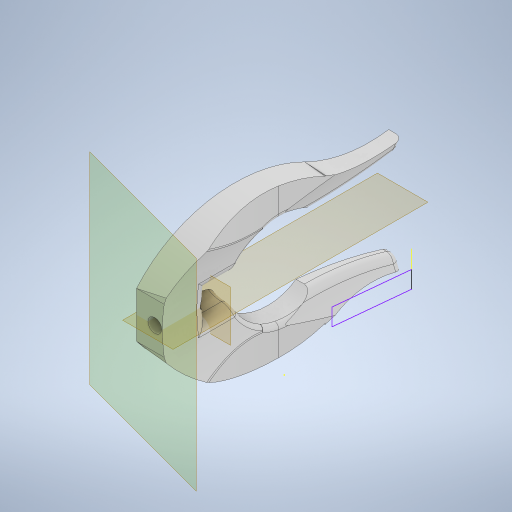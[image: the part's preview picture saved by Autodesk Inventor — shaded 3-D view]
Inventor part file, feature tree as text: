
AUTODESK INVENTOR PART (.ipt)
format: ipt  version: 2024.2 (Build 282272000, 272)  size: 638,464 bytes
history: native  units: mm
features: sketch x10, extrude x9, fillet x5, plane x3, mirror x1
ambient origin geometry x8: Origin, YZ Plane, XZ Plane, XY Plane, X Axis, Y Axis, Z Axis, Center Point
bodies: Solid1 (feature_tree)
feature tree (28):
  extrude  "Extrusion1"  Depth=80.0mm TaperAngle=0.0deg
  extrude  "Extrusion2"  Depth=40.0mm
  extrude  "Extrusion3"  Depth=30.0mm
  plane  "Work Plane2"
  extrude  "Extrusion6"  Depth=10.0mm
  extrude  "Extrusion7"  Depth=10.0mm
  plane  "Work Plane3"
  extrude  "Extrusion8"  Depth=6.0mm
  sketch  "Sketch10"  dims[d20=12.0mm d21=0.0mm d22=0.0mm d29=165.0deg]
  extrude  "Extrusion9"  TaperAngle=0.0deg  [1 undecoded]
  fillet  "Fillet3"  [1 undecoded]
  extrude  "Extrusion10"  TaperAngle=0.0deg  [1 undecoded]
  fillet  "Fillet4"  Radius=120.0mm
  fillet  "Fillet5"  [1 undecoded]
  fillet  "Fillet6"  [1 undecoded]
  fillet  "Fillet7"  Radius=12.0mm
  extrude  "Extrusion11"  Depth=10.0mm TaperAngle=0.0deg
  plane  "Work Plane4"
  mirror  "Mirror1"
  sketch  "Sketch1"  dims[d0=20.0mm d1=100.0mm d3=80.0mm d4=0.0mm]
  sketch  "Sketch2"  dims[d6=5.0mm d7=40.0mm]
  sketch  "Sketch3"  dims[d8=20.0mm d9=30.0mm]
  sketch  "Sketch7"  dims[d13=50.0mm d14=10.0mm]
  sketch  "Sketch8"  dims[d15=50.0mm d16=10.0mm]
  sketch  "Sketch9"  dims[d17=80.0mm d18=0.0mm d19=6.0mm]
  sketch  "Sketch11"  dims[d41=240.0mm d42=0.0mm d43=0.0mm d44=120.0mm d45=0.0mm d46=0.0mm d47=-20.0mm d48=12.0mm]
  sketch  "Sketch12"  dims[d49=0.0mm d50=0.0mm d51=10.0mm d52=0.0mm]
  sketch  "Sketch13"  dims[d53=2.0mm d54=65.0mm d55=65.0mm d56=0.0mm d57=0.0mm d58=4.0mm d59=3.0mm d60=5.0mm d61=2.0mm d62=55.0mm d63=50.0mm d64=0.0mm d65=0.0mm d66=40.0mm]
note: 5 required parameter values undecoded (feature->parameter linkage not recoverable at this tier; creation-order binding heuristic only, values carry confidence <= 0.55)
